FCSTD DOCUMENT  (FreeCAD 0.16R6712 (Git))
Label: Support_Composants
License: All rights reserved
LicenseURL: http://en.wikipedia.org/wiki/All_rights_reserved
objects: Sketcher::SketchObject×20, PartDesign::Pad×12, PartDesign::Pocket×8, Mesh::Feature×6
note: 60 computed .brp shape members not serialized (recipe doc carries the construction recipe); baked Part::Feature solids carry a one-line shape summary decoded from their .brp

FEATURE [Sketcher::SketchObject] Sketch
  sketch-geometry (4):
    g0: LineSegment StartX=0 StartY=1 StartZ=0 EndX=69 EndY=1 EndZ=0
    g1: LineSegment StartX=69 StartY=1 StartZ=0 EndX=69 EndY=0 EndZ=0
    g2: LineSegment StartX=69 StartY=0 StartZ=0 EndX=0 EndY=0 EndZ=0
    g3: LineSegment StartX=0 StartY=0 StartZ=0 EndX=0 EndY=1 EndZ=0
  constraints (11):
    c: Coincident(g0,g1)
    c: Coincident(g1,g2)
    c: Coincident(g2,g3)
    c: Coincident(g3,g0)
    c: Horizontal(g0)
    c: Horizontal(g2)
    c: Vertical(g1)
    c: Vertical(g3)
    c: DistanceX(g2,g2) = 69
    c: DistanceY(g1,g1) = 1
    c: Coincident(g2,g-1)
FEATURE [PartDesign::Pad] Pad
  Length = 120
  Length2 = 100
  Sketch = -> Sketch
  Type = 0
FEATURE [Sketcher::SketchObject] Sketch001
  ExternalGeometry = -> [Pad]
  Placement = pos=(0,1,0) rot=(0,0.707107,0.707107;3.14159rad)
  Support = -> Pad [Face1]
  sketch-geometry (9):
    g0: LineSegment StartX=-69 StartY=26 StartZ=0 EndX=0 EndY=26 EndZ=0
    g1: LineSegment StartX=0 StartY=26 StartZ=0 EndX=0 EndY=24 EndZ=0
    g2: LineSegment StartX=0 StartY=24 StartZ=0 EndX=-69 EndY=24 EndZ=0
    g3: LineSegment StartX=-69 StartY=24 StartZ=0 EndX=-69 EndY=26 EndZ=0
    g4: LineSegment StartX=-69 StartY=96 StartZ=0 EndX=0 EndY=96 EndZ=0
    g5: LineSegment StartX=0 StartY=96 StartZ=0 EndX=0 EndY=94 EndZ=0
    g6: LineSegment StartX=0 StartY=94 StartZ=0 EndX=-69 EndY=94 EndZ=0
    g7: LineSegment StartX=-69 StartY=94 StartZ=0 EndX=-69 EndY=96 EndZ=0
    g8: LineSegment [constr] StartX=-69 StartY=60 StartZ=0 EndX=0 EndY=60 EndZ=0
  constraints (27):
    c: Coincident(g0,g1)
    c: Coincident(g1,g2)
    c: Coincident(g2,g3)
    c: Coincident(g3,g0)
    c: Horizontal(g0)
    c: Horizontal(g2)
    c: Vertical(g1)
    c: Vertical(g3)
    c: Coincident(g4,g5)
    c: Coincident(g5,g6)
    c: Coincident(g6,g7)
    c: Coincident(g7,g4)
    c: Horizontal(g4)
    c: Horizontal(g6)
    c: Vertical(g5)
    c: Vertical(g7)
    c: PointOnObject(g8,g-3)
    c: PointOnObject(g8,g-4)
    c: Symmetric(g-4,g-4,g8)
    c: DistanceY(g7,g7) = 2
    c: DistanceY(g3,g3) = 2
    c: PointOnObject(g4,g-3)
    c: PointOnObject(g4,g-4)
    c: PointOnObject(g0,g-4)
    c: PointOnObject(g0,g-3)
    c: Symmetric(g5,g0,g8)
    c: DistanceY(g0,g5) = 68
FEATURE [PartDesign::Pad] Pad001
  Length = 1
  Length2 = 100
  Sketch = -> Sketch001
  Type = 0
FEATURE [Sketcher::SketchObject] Sketch002
  ExternalGeometry = -> [Pad001]
  Placement = pos=(0,1,0) rot=(0,0.707107,0.707107;3.14159rad)
  Support = -> Pad001 [Face8]
  sketch-geometry (4):
    g0: LineSegment StartX=-2 StartY=94 StartZ=0 EndX=0 EndY=94 EndZ=0
    g1: LineSegment StartX=0 StartY=94 StartZ=0 EndX=0 EndY=26 EndZ=0
    g2: LineSegment StartX=0 StartY=26 StartZ=0 EndX=-2 EndY=26 EndZ=0
    g3: LineSegment StartX=-2 StartY=26 StartZ=0 EndX=-2 EndY=94 EndZ=0
  constraints (12):
    c: Coincident(g0,g1)
    c: Coincident(g1,g2)
    c: Coincident(g2,g3)
    c: Coincident(g3,g0)
    c: Horizontal(g0)
    c: Horizontal(g2)
    c: Vertical(g1)
    c: Vertical(g3)
    c: PointOnObject(g1,g-3)
    c: Coincident(g0,g-3)
    c: Coincident(g1,g-3)
    c: DistanceX(g2,g2) = 2
FEATURE [PartDesign::Pad] Pad002
  Length = 17
  Length2 = 100
  Sketch = -> Sketch002
  Type = 0
FEATURE [Sketcher::SketchObject] Sketch004
  ExternalGeometry = -> [Pad002]
  Placement = pos=(0,18,0) rot=(0,0.707107,0.707107;3.14159rad)
  Support = -> Pad002 [Face22]
  sketch-geometry (5):
    g0: LineSegment StartX=-39 StartY=116 StartZ=0 EndX=0 EndY=116 EndZ=0
    g1: LineSegment StartX=0 StartY=116 StartZ=0 EndX=0 EndY=4 EndZ=0
    g2: LineSegment StartX=0 StartY=4 StartZ=0 EndX=-39 EndY=4 EndZ=0
    g3: LineSegment StartX=-39 StartY=4 StartZ=0 EndX=-39 EndY=116 EndZ=0
    g4: LineSegment [constr] StartX=-39 StartY=60 StartZ=0 EndX=0 EndY=60 EndZ=0
  constraints (15):
    c: Coincident(g0,g1)
    c: Coincident(g1,g2)
    c: Coincident(g2,g3)
    c: Coincident(g3,g0)
    c: Horizontal(g0)
    c: Horizontal(g2)
    c: Vertical(g1)
    c: Vertical(g3)
    c: DistanceY(g3,g3) = 112
    c: DistanceX(g0,g0) = 39
    c: PointOnObject(g4,g3)
    c: Symmetric(g1,g0,g4)
    c: PointOnObject(g-3,g1)
    c: PointOnObject(g4,g-3)
    c: Symmetric(g-3,g-3,g4)
FEATURE [PartDesign::Pad] Pad003
  Length = 2
  Length2 = 100
  Sketch = -> Sketch004
  Type = 0
FEATURE [Sketcher::SketchObject] Sketch005
  ExternalGeometry = -> [Pad003]
  Placement = pos=(0,0,4) rot=(1,0,0;3.14159rad)
  Support = -> Pad003 [Face27]
  sketch-geometry (4):
    g0: LineSegment StartX=0 StartY=-18 StartZ=0 EndX=0 EndY=-1 EndZ=0
    g1: LineSegment StartX=0 StartY=-18 StartZ=0 EndX=39 EndY=-18 EndZ=0
    g2: LineSegment StartX=0 StartY=-1 StartZ=0 EndX=7 EndY=-1 EndZ=0
    g3: ArcOfCircle CenterX=39 CenterY=20.6177 CenterZ=0 NormalX=0 NormalY=0 NormalZ=1 Radius=38.6177 StartAngle=3.73572 EndAngle=4.71239
  constraints (12):
    c: Coincident(g0,g2)
    c: Horizontal(g2)
    c: Coincident(g0,g1)
    c: Horizontal(g1)
    c: Vertical(g0)
    c: DistanceX(g0,g2) = 7
    c: Coincident(g3,g1)
    c: Coincident(g3,g2)
    c: DistanceY(g0,g0) = 17
    c: Coincident(g1,g-3)
    c: Coincident(g0,g-3)
    c: Tangent(g-3,g3)
FEATURE [PartDesign::Pad] Pad004
  Length = 2
  Length2 = 100
  Reversed = true
  Sketch = -> Sketch005
  Type = 0
FEATURE [Sketcher::SketchObject] Sketch006
  ExternalGeometry = -> [Pad004]
  Placement = pos=(0,0,116) rot=(0,0,1;0rad)
  Support = -> Pad004 [Face31]
  sketch-geometry (4):
    g0: LineSegment StartX=0 StartY=18 StartZ=0 EndX=0 EndY=1 EndZ=0
    g1: LineSegment StartX=0 StartY=1 StartZ=0 EndX=7 EndY=1 EndZ=0
    g2: LineSegment StartX=0 StartY=18 StartZ=0 EndX=39 EndY=18 EndZ=0
    g3: ArcOfCircle CenterX=39 CenterY=-20.6177 CenterZ=0 NormalX=0 NormalY=0 NormalZ=1 Radius=38.6177 StartAngle=1.5708 EndAngle=2.54746
  constraints (12):
    c: Vertical(g0)
    c: Coincident(g1,g0)
    c: Horizontal(g1)
    c: Horizontal(g2)
    c: Coincident(g2,g0)
    c: DistanceY(g0,g0) = 17
    c: DistanceX(g1,g1) = 7
    c: Coincident(g3,g2)
    c: Coincident(g3,g1)
    c: Coincident(g2,g-3)
    c: Coincident(g0,g-3)
    c: Tangent(g3,g-3)
FEATURE [PartDesign::Pad] Pad005
  Length = 2
  Length2 = 100
  Reversed = true
  Sketch = -> Sketch006
  Type = 0
FEATURE [Sketcher::SketchObject] Sketch007
  ExternalGeometry = -> [Pad005]
  Placement = pos=(0,0,0) rot=(0.57735,-0.57735,-0.57735;2.0944rad)
  Support = -> Pad005 [Face19]
  sketch-geometry (4):
    g0: LineSegment StartX=-15 StartY=74 StartZ=0 EndX=-2 EndY=74 EndZ=0
    g1: LineSegment StartX=-15 StartY=36 StartZ=0 EndX=-2 EndY=36 EndZ=0
    g2: LineSegment StartX=-15 StartY=74 StartZ=0 EndX=-15 EndY=36 EndZ=0
    g3: LineSegment StartX=-2 StartY=74 StartZ=0 EndX=-2 EndY=36 EndZ=0
  constraints (12):
    c: Horizontal(g0)
    c: Horizontal(g1)
    c: Coincident(g2,g0)
    c: Coincident(g2,g1)
    c: Vertical(g2)
    c: Coincident(g3,g0)
    c: Coincident(g3,g1)
    c: Vertical(g3)
    c: DistanceY(g0,g-3) = 20
    c: DistanceX(g0,g-3) = 1
    c: DistanceY(g-4,g1) = 10
    c: DistanceX(g-4,g1) = 3
FEATURE [PartDesign::Pocket] Pocket
  Length = 5
  Sketch = -> Sketch007
  Type = 2
FEATURE [Sketcher::SketchObject] Sketch008
  ExternalGeometry = -> [Pocket]
  Placement = pos=(0,20,0) rot=(0,0.707107,0.707107;3.14159rad)
  Support = -> Pocket [Face39]
  sketch-geometry (8):
    g0: LineSegment StartX=0 StartY=116 StartZ=0 EndX=-2 EndY=116 EndZ=0
    g1: LineSegment StartX=-2 StartY=116 StartZ=0 EndX=-2 EndY=6 EndZ=0
    g2: LineSegment StartX=0 StartY=4 StartZ=0 EndX=0 EndY=116 EndZ=0
    g3: LineSegment StartX=-39 StartY=4 StartZ=0 EndX=0 EndY=4 EndZ=0
    g4: LineSegment StartX=-2 StartY=6 StartZ=0 EndX=-37 EndY=6 EndZ=0
    g5: LineSegment StartX=-39 StartY=116 StartZ=0 EndX=-37 EndY=116 EndZ=0
    g6: LineSegment StartX=-37 StartY=116 StartZ=0 EndX=-37 EndY=6 EndZ=0
    g7: LineSegment StartX=-39 StartY=116 StartZ=0 EndX=-39 EndY=4 EndZ=0
  constraints (22):
    c: Coincident(g0,g1)
    c: Coincident(g2,g0)
    c: Horizontal(g0)
    c: Vertical(g1)
    c: Vertical(g2)
    c: Horizontal(g3)
    c: Horizontal(g4)
    c: Coincident(g4,g1)
    c: DistanceX(g0,g0) = 2
    c: Coincident(g5,g6)
    c: Horizontal(g5)
    c: Vertical(g6)
    c: Coincident(g4,g6)
    c: DistanceY(g3,g1) = 2
    c: Coincident(g2,g3)
    c: Coincident(g7,g5)
    c: Coincident(g7,g3)
    c: DistanceX(g5,g5) = 2
    c: Coincident(g5,g-4)
    c: Coincident(g0,g-3)
    c: Coincident(g-3,g2)
    c: Coincident(g3,g-4)
FEATURE [PartDesign::Pad] Pad006
  Length = 25
  Length2 = 100
  Sketch = -> Sketch008
  Type = 0
FEATURE [Sketcher::SketchObject] Sketch010
  ExternalGeometry = -> [Pad006]
  Placement = pos=(0,0,0) rot=(0.57735,-0.57735,-0.57735;2.0944rad)
  Support = -> Pad006 [Face12]
  sketch-geometry (5):
    g0: LineSegment StartX=-20 StartY=120 StartZ=0 EndX=-18 EndY=120 EndZ=0
    g1: LineSegment StartX=-18 StartY=120 StartZ=0 EndX=-18 EndY=0 EndZ=0
    g2: LineSegment StartX=-18 StartY=0 StartZ=0 EndX=-20 EndY=0 EndZ=0
    g3: LineSegment StartX=-20 StartY=0 StartZ=0 EndX=-20 EndY=120 EndZ=0
    g4: LineSegment [constr] StartX=-18 StartY=120 StartZ=0 EndX=-1 EndY=120 EndZ=0
  constraints (14):
    c: Coincident(g0,g1)
    c: Coincident(g1,g2)
    c: Coincident(g2,g3)
    c: Coincident(g3,g0)
    c: Horizontal(g0)
    c: Horizontal(g2)
    c: Vertical(g1)
    c: Vertical(g3)
    c: PointOnObject(g1,g-1)
    c: Coincident(g4,g0)
    c: Coincident(g4,g-3)
    c: Horizontal(g4)
    c: DistanceX(g0,g0) = 2
    c: PointOnObject(g-4,g1)
FEATURE [PartDesign::Pad] Pad007
  Length = 100
  Length2 = 100
  Reversed = true
  Sketch = -> Sketch010
  Type = 0
FEATURE [Sketcher::SketchObject] Sketch011
  ExternalGeometry = -> [Pad007]
  Placement = pos=(0,20,0) rot=(0,0.707107,0.707107;3.14159rad)
  Support = -> Pad007 [Face10]
  sketch-geometry (20):
    g0: LineSegment StartX=-69 StartY=10 StartZ=0 EndX=-74 EndY=10 EndZ=0
    g1: LineSegment StartX=-74 StartY=10 StartZ=0 EndX=-74 EndY=5 EndZ=0
    g2: LineSegment StartX=-74 StartY=5 StartZ=0 EndX=-69 EndY=5 EndZ=0
    g3: LineSegment StartX=-69 StartY=5 StartZ=0 EndX=-69 EndY=10 EndZ=0
    g4: LineSegment StartX=-49 StartY=10 StartZ=0 EndX=-44 EndY=10 EndZ=0
    g5: LineSegment StartX=-44 StartY=10 StartZ=0 EndX=-44 EndY=5 EndZ=0
    g6: LineSegment StartX=-44 StartY=5 StartZ=0 EndX=-49 EndY=5 EndZ=0
    g7: LineSegment StartX=-49 StartY=5 StartZ=0 EndX=-49 EndY=10 EndZ=0
    g8: LineSegment StartX=-74 StartY=115 StartZ=0 EndX=-69 EndY=115 EndZ=0
    g9: LineSegment StartX=-69 StartY=115 StartZ=0 EndX=-69 EndY=110 EndZ=0
    g10: LineSegment StartX=-69 StartY=110 StartZ=0 EndX=-74 EndY=110 EndZ=0
    g11: LineSegment StartX=-74 StartY=110 StartZ=0 EndX=-74 EndY=115 EndZ=0
    g12: LineSegment StartX=-49 StartY=115 StartZ=0 EndX=-44 EndY=115 EndZ=0
    g13: LineSegment StartX=-44 StartY=115 StartZ=0 EndX=-44 EndY=110 EndZ=0
    g14: LineSegment StartX=-44 StartY=110 StartZ=0 EndX=-49 EndY=110 EndZ=0
    g15: LineSegment StartX=-49 StartY=110 StartZ=0 EndX=-49 EndY=115 EndZ=0
    g16: LineSegment [constr] StartX=-69 StartY=110 StartZ=0 EndX=-49 EndY=110 EndZ=0
    g17: LineSegment [constr] StartX=-74 StartY=5 StartZ=0 EndX=-49 EndY=5 EndZ=0
    g18: LineSegment [constr] StartX=-69 StartY=10 StartZ=0 EndX=-49 EndY=10 EndZ=0
    g19: LineSegment [constr] StartX=-69 StartY=115 StartZ=0 EndX=-49 EndY=115 EndZ=0
  constraints (56):
    c: Coincident(g0,g1)
    c: Coincident(g1,g2)
    c: Coincident(g2,g3)
    c: Coincident(g3,g0)
    c: Horizontal(g0)
    c: Horizontal(g2)
    c: Vertical(g1)
    c: Vertical(g3)
    c: Coincident(g4,g5)
    c: Coincident(g5,g6)
    c: Coincident(g6,g7)
    c: Coincident(g7,g4)
    c: Horizontal(g4)
    c: Horizontal(g6)
    c: Vertical(g5)
    c: Vertical(g7)
    c: Coincident(g8,g9)
    c: Coincident(g9,g10)
    c: Coincident(g10,g11)
    c: Coincident(g11,g8)
    c: Horizontal(g8)
    c: Horizontal(g10)
    c: Vertical(g9)
    c: Vertical(g11)
    c: Coincident(g12,g13)
    c: Coincident(g13,g14)
    c: Coincident(g14,g15)
    c: Coincident(g15,g12)
    c: Horizontal(g12)
    c: Horizontal(g14)
    c: Vertical(g13)
    c: Vertical(g15)
    c: Coincident(g16,g9)
    c: Coincident(g16,g14)
    c: Horizontal(g16)
    c: Coincident(g17,g1)
    c: Coincident(g17,g6)
    c: Horizontal(g17)
    c: DistanceX(g2,g2) = 5
    c: DistanceX(g6,g6) = 5
    c: DistanceX(g10,g10) = 5
    c: DistanceX(g16,g16) = 20
    c: DistanceX(g14,g14) = 5
    c: DistanceY(g12,g-4) = 5
    c: DistanceY(g-1,g5) = 5
    c: Coincident(g18,g0)
    c: Coincident(g18,g4)
    c: Horizontal(g18)
    c: Coincident(g19,g12)
    c: Horizontal(g19)
    c: Coincident(g19,g8)
    c: DistanceY(g1,g1) = 5
    c: DistanceY(g11,g11) = 5
    c: DistanceX(g0,g4) = 20
    c: DistanceX(g5,g-5) = 5
    c: DistanceX(g12,g-5) = 5
FEATURE [PartDesign::Pad] Pad008
  Length = 10
  Length2 = 100
  Sketch = -> Sketch011
  Type = 0
FEATURE [Mesh::Feature] Servo_CYS
  Placement = pos=(69,20,19) rot=(0,1,0;3.14159rad)
FEATURE [Mesh::Feature] Servo_CYS001
  Placement = pos=(49,20,101) rot=(0,0,1;0rad)
FEATURE [Mesh::Feature] ESC
  Placement = pos=(67,1,94) rot=(-1,0,0;1.5708rad)
FEATURE [Sketcher::SketchObject] Sketch012
  ExternalGeometry = -> [Pad008]
  Placement = pos=(0,20,0) rot=(0,0.707107,0.707107;3.14159rad)
  Support = -> Pad008 [Face10]
  sketch-geometry (7):
    g0: Circle CenterX=-85 CenterY=75.25 CenterZ=0 NormalX=0 NormalY=0 NormalZ=1 Radius=4
    g1: Circle CenterX=-54.5 CenterY=75.25 CenterZ=0 NormalX=0 NormalY=0 NormalZ=1 Radius=4
    g2: Circle CenterX=-85 CenterY=44.75 CenterZ=0 NormalX=0 NormalY=0 NormalZ=1 Radius=4
    g3: Circle CenterX=-54.5 CenterY=44.75 CenterZ=0 NormalX=0 NormalY=0 NormalZ=1 Radius=4
    g4: LineSegment [constr] StartX=-85 StartY=75.25 StartZ=0 EndX=-54.5 EndY=75.25 EndZ=0
    g5: LineSegment [constr] StartX=-85 StartY=75.25 StartZ=0 EndX=-85 EndY=44.75 EndZ=0
    g6: LineSegment [constr] StartX=-100 StartY=60 StartZ=0 EndX=0 EndY=60 EndZ=0
  constraints (19):
    c: DistanceY(g3,g1) = 30.5
    c: DistanceX(g2,g3) = 30.5
    c: DistanceY(g2,g0) = 30.5
    c: DistanceX(g0,g1) = 30.5
    c: Coincident(g4,g0)
    c: Coincident(g4,g1)
    c: Coincident(g5,g0)
    c: Coincident(g5,g2)
    c: Vertical(g5)
    c: Horizontal(g4)
    c: Radius(g0) = 4
    c: Equal(g0,g1)
    c: Equal(g0,g3)
    c: Equal(g0,g2)
    c: PointOnObject(g6,g-2)
    c: PointOnObject(g6,g-5)
    c: Symmetric(g2,g0,g6)
    c: Symmetric(g-5,g-5,g6)
    c: DistanceX(g-5,g0) = 15
FEATURE [PartDesign::Pad] Pad009
  Length = 4
  Length2 = 100
  Sketch = -> Sketch012
  Type = 0
FEATURE [Sketcher::SketchObject] Sketch013
  ExternalGeometry = -> [Pad009]
  Placement = pos=(0,0,0) rot=(1,0,0;1.5708rad)
  Support = -> Pad009 [Face68]
  sketch-geometry (7):
    g0: Circle CenterX=54.5 CenterY=75.25 CenterZ=0 NormalX=0 NormalY=0 NormalZ=1 Radius=3
    g1: Circle CenterX=85 CenterY=75.25 CenterZ=0 NormalX=0 NormalY=0 NormalZ=1 Radius=3
    g2: Circle CenterX=54.5 CenterY=44.75 CenterZ=0 NormalX=0 NormalY=0 NormalZ=1 Radius=3
    g3: Circle CenterX=85 CenterY=44.75 CenterZ=0 NormalX=0 NormalY=0 NormalZ=1 Radius=3
    g4: LineSegment [constr] StartX=54.5 StartY=44.75 StartZ=0 EndX=85 EndY=44.75 EndZ=0
    g5: LineSegment [constr] StartX=54.5 StartY=75.25 StartZ=0 EndX=54.5 EndY=44.75 EndZ=0
    g6: LineSegment [constr] StartX=0 StartY=60 StartZ=0 EndX=100 EndY=60 EndZ=0
  constraints (19):
    c: Coincident(g4,g2)
    c: Coincident(g4,g3)
    c: Coincident(g5,g0)
    c: Coincident(g5,g2)
    c: Vertical(g5)
    c: Horizontal(g4)
    c: DistanceY(g3,g1) = 30.5
    c: DistanceX(g4,g4) = 30.5
    c: DistanceY(g5,g5) = 30.5
    c: DistanceX(g0,g1) = 30.5
    c: PointOnObject(g6,g-3)
    c: PointOnObject(g6,g-4)
    c: Symmetric(g-4,g-4,g6)
    c: Symmetric(g3,g1,g6)
    c: Radius(g1) = 3
    c: Equal(g1,g2)
    c: Equal(g1,g3)
    c: Equal(g1,g0)
    c: DistanceX(g1,g-4) = 15
FEATURE [PartDesign::Pocket] Pocket001
  Length = 21
  Sketch = -> Sketch013
  Type = 0
FEATURE [Sketcher::SketchObject] Sketch014
  ExternalGeometry = -> [Pocket001]
  Placement = pos=(0,24,0) rot=(0,0.707107,0.707107;3.14159rad)
  Support = -> Pocket001 [Face49]
  sketch-geometry (4):
    g0: Circle CenterX=-85 CenterY=75.25 CenterZ=0 NormalX=0 NormalY=0 NormalZ=1 Radius=1.7
    g1: Circle CenterX=-54.5 CenterY=75.25 CenterZ=0 NormalX=0 NormalY=0 NormalZ=1 Radius=1.7
    g2: Circle CenterX=-85 CenterY=44.75 CenterZ=0 NormalX=0 NormalY=0 NormalZ=1 Radius=1.7
    g3: Circle CenterX=-54.5 CenterY=44.75 CenterZ=0 NormalX=0 NormalY=0 NormalZ=1 Radius=1.7
  constraints (8):
    c: Coincident(g0,g-3)
    c: Coincident(g1,g-4)
    c: Coincident(g2,g-5)
    c: Coincident(g3,g-6)
    c: Radius(g3) = 1.7
    c: Equal(g3,g1)
    c: Equal(g3,g0)
    c: Equal(g3,g2)
FEATURE [PartDesign::Pocket] Pocket002
  Length = 5
  Sketch = -> Sketch014
  Type = 1
FEATURE [Mesh::Feature] Carte_SPRACINGF3
  Placement = pos=(88,24,42) rot=(0,0.707107,0.707107;3.14159rad)
FEATURE [Mesh::Feature] Recepteur
  Placement = pos=(43,27,19) rot=(1,0,0;1.5708rad)
FEATURE [Mesh::Feature] Batterie
  Placement = pos=(3,23,6) rot=(0,0,1;0rad)
FEATURE [Sketcher::SketchObject] Sketch015
  ExternalGeometry = -> [Pocket002]
  Placement = pos=(0,0,120) rot=(0,0,1;0rad)
  Support = -> Pocket002 [Face78]
  sketch-geometry (4):
    g0: LineSegment StartX=62.2327 StartY=4.2e-11 StartZ=0 EndX=100 EndY=0 EndZ=0
    g1: LineSegment StartX=100 StartY=0 StartZ=0 EndX=100 EndY=18 EndZ=0
    g2: LineSegment StartX=85 StartY=18 StartZ=0 EndX=100 EndY=18 EndZ=0
    g3: ArcOfCircle CenterX=62.2326 CenterY=23.3987 CenterZ=0 NormalX=0 NormalY=0 NormalZ=1 Radius=23.3987 StartAngle=4.71239 EndAngle=6.05036
  constraints (12):
    c: PointOnObject(g0,g-1)
    c: Coincident(g1,g0)
    c: Vertical(g1)
    c: Coincident(g1,g-3)
    c: PointOnObject(g2,g-3)
    c: Coincident(g2,g1)
    c: PointOnObject(g0,g-4)
    c: Coincident(g3,g2)
    c: Coincident(g3,g0)
    c: Tangent(g3,g0)
    c: PointOnObject(g-5,g3)
    c: DistanceX(g2,g1) = 15
FEATURE [PartDesign::Pad] Pad010
  Length = 2
  Length2 = 100
  Reversed = true
  Sketch = -> Sketch015
  Type = 0
FEATURE [Sketcher::SketchObject] Sketch016
  ExternalGeometry = -> [Pad010]
  Placement = pos=(0,0,0) rot=(1,0,0;3.14159rad)
  Support = -> Pad010 [Face83]
  sketch-geometry (4):
    g0: LineSegment StartX=62.2326 StartY=0 StartZ=0 EndX=100 EndY=0 EndZ=0
    g1: LineSegment StartX=100 StartY=0 StartZ=0 EndX=100 EndY=-18 EndZ=0
    g2: LineSegment StartX=100 StartY=-18 StartZ=0 EndX=85 EndY=-18 EndZ=0
    g3: ArcOfCircle CenterX=62.2326 CenterY=-23.3987 CenterZ=0 NormalX=0 NormalY=0 NormalZ=1 Radius=23.3987 StartAngle=0.232825 EndAngle=1.5708
  constraints (14):
    c: PointOnObject(g0,g-1)
    c: PointOnObject(g0,g-1)
    c: Vertical(g1)
    c: Horizontal(g2)
    c: PointOnObject(g3,g0)
    c: Coincident(g3,g0)
    c: Coincident(g3,g2)
    c: PointOnObject(g-6,g3)
    c: Tangent(g3,g0)
    c: PointOnObject(g2,g-3)
    c: Coincident(g2,g1)
    c: Coincident(g2,g-3)
    c: DistanceX(g2,g1) = 15
    c: Coincident(g0,g1)
FEATURE [PartDesign::Pad] Pad011
  Length = 2
  Length2 = 100
  Reversed = true
  Sketch = -> Sketch016
  Type = 0
FEATURE [Sketcher::SketchObject] Sketch017
  ExternalGeometry = -> [Pad011]
  Placement = pos=(0,0,0) rot=(1,0,0;3.14159rad)
  Support = -> Pad011 [Face43]
  sketch-geometry (4):
    g0: LineSegment StartX=90 StartY=0 StartZ=0 EndX=100 EndY=0 EndZ=0
    g1: LineSegment StartX=100 StartY=0 StartZ=0 EndX=100 EndY=-20 EndZ=0
    g2: LineSegment StartX=100 StartY=-20 StartZ=0 EndX=90 EndY=-20 EndZ=0
    g3: LineSegment StartX=90 StartY=-20 StartZ=0 EndX=90 EndY=0 EndZ=0
  constraints (11):
    c: Coincident(g0,g1)
    c: Coincident(g1,g2)
    c: Coincident(g2,g3)
    c: Coincident(g3,g0)
    c: Horizontal(g0)
    c: Horizontal(g2)
    c: Vertical(g1)
    c: Vertical(g3)
    c: PointOnObject(g0,g-1)
    c: Coincident(g1,g-4)
    c: DistanceX(g2,g1) = 10
FEATURE [PartDesign::Pocket] Pocket003
  Length = 5
  Sketch = -> Sketch017
  Type = 1
FEATURE [Sketcher::SketchObject] Sketch018
  ExternalGeometry = -> [Pocket003]
  Placement = pos=(0,0,115) rot=(0,0,1;0rad)
  Support = -> Pocket003 [Face32]
  sketch-geometry (3):
    g0: Circle CenterX=47.4 CenterY=24.2 CenterZ=0 NormalX=0 NormalY=0 NormalZ=1 Radius=0.75
    g1: Circle CenterX=70.4 CenterY=24.2 CenterZ=0 NormalX=0 NormalY=0 NormalZ=1 Radius=0.75
    g2: LineSegment [constr] StartX=47.4 StartY=24.2 StartZ=0 EndX=70.4 EndY=24.2 EndZ=0
  constraints (8):
    c: Radius(g1) = 0.75
    c: Radius(g0) = 0.75
    c: DistanceX(g0,g1) = 23
    c: DistanceX(g-4,g1) = 1.4
    c: Coincident(g2,g0)
    c: Coincident(g2,g1)
    c: Horizontal(g2)
    c: DistanceY(g0,g-3) = 5.8
FEATURE [PartDesign::Pocket] Pocket004
  Length = 5
  Sketch = -> Sketch018
  Type = 1
FEATURE [Sketcher::SketchObject] Sketch019
  ExternalGeometry = -> [Pocket004]
  Placement = pos=(0,20,0) rot=(0,0.707107,0.707107;3.14159rad)
  Support = -> Pocket004 [Face10]
  sketch-geometry (17):
    g0: LineSegment StartX=-77 StartY=100 StartZ=0 EndX=-41 EndY=100 EndZ=0
    g1: LineSegment StartX=-41 StartY=100 StartZ=0 EndX=-41 EndY=82 EndZ=0
    g2: LineSegment StartX=-41 StartY=82 StartZ=0 EndX=-86 EndY=82 EndZ=0
    g3: LineSegment StartX=-86 StartY=82 StartZ=0 EndX=-86 EndY=100 EndZ=0
    g4: LineSegment StartX=-86 StartY=67 StartZ=0 EndX=-41 EndY=67 EndZ=0
    g5: LineSegment StartX=-41 StartY=67 StartZ=0 EndX=-41 EndY=52 EndZ=0
    g6: LineSegment StartX=-41 StartY=52 StartZ=0 EndX=-86 EndY=52 EndZ=0
    g7: LineSegment StartX=-86 StartY=52 StartZ=0 EndX=-86 EndY=67 EndZ=0
    g8: LineSegment StartX=-77 StartY=100 StartZ=0 EndX=-77 EndY=116 EndZ=0
    g9: LineSegment StartX=-77 StartY=116 StartZ=0 EndX=-86 EndY=116 EndZ=0
    g10: LineSegment StartX=-86 StartY=116 StartZ=0 EndX=-86 EndY=100 EndZ=0
    g11: LineSegment StartX=-86 StartY=4 StartZ=0 EndX=-86 EndY=37 EndZ=0
    g12: LineSegment StartX=-86 StartY=37 StartZ=0 EndX=-45 EndY=37 EndZ=0
    g13: LineSegment StartX=-45 StartY=37 StartZ=0 EndX=-45 EndY=22 EndZ=0
    g14: LineSegment StartX=-77 StartY=22 StartZ=0 EndX=-45 EndY=22 EndZ=0
    g15: LineSegment StartX=-77 StartY=22 StartZ=0 EndX=-77 EndY=4 EndZ=0
    g16: LineSegment StartX=-77 StartY=4 StartZ=0 EndX=-86 EndY=4 EndZ=0
  constraints (52):
    c: Coincident(g0,g1)
    c: Coincident(g1,g2)
    c: Coincident(g2,g3)
    c: Horizontal(g0)
    c: Horizontal(g2)
    c: Vertical(g1)
    c: Vertical(g3)
    c: DistanceX(g-3,g3) = 4
    c: DistanceX(g0,g-5) = 2
    c: DistanceY(g3,g-3) = 20
    c: DistanceY(g3,g3) = 18
    c: Coincident(g4,g5)
    c: Coincident(g5,g6)
    c: Coincident(g6,g7)
    c: Coincident(g7,g4)
    c: Horizontal(g4)
    c: Horizontal(g6)
    c: Vertical(g5)
    c: Vertical(g7)
    c: DistanceY(g4,g2) = 15
    c: DistanceX(g4,g-5) = 2
    c: DistanceX(g-3,g4) = 4
    c: DistanceY(g7,g7) = 15
    c: Coincident(g8,g9)
    c: Coincident(g9,g10)
    c: Horizontal(g9)
    c: Vertical(g8)
    c: Vertical(g10)
    c: PointOnObject(g0,g8)
    c: DistanceY(g9,g-3) = 4
    c: DistanceX(g9,g9) = 9
    c: Coincident(g3,g10)
    c: Coincident(g0,g8)
    c: DistanceY(g8,g8) = 16
    c: Coincident(g12,g11)
    c: Horizontal(g12)
    c: Vertical(g13)
    c: Horizontal(g14)
    c: Coincident(g16,g11)
    c: Vertical(g11)
    c: Coincident(g14,g15)
    c: Vertical(g15)
    c: Coincident(g15,g16)
    c: Horizontal(g16)
    c: DistanceX(g-3,g11) = 4
    c: DistanceY(g11,g6) = 15
    c: Coincident(g13,g12)
    c: Coincident(g14,g13)
    c: DistanceY(g13,g13) = 15
    c: DistanceY(g-3,g11) = 4
    c: DistanceX(g16,g16) = 9
    c: DistanceX(g13,g-5) = 6
FEATURE [PartDesign::Pocket] Pocket005
  Length = 0
  Sketch = -> Sketch019
  Type = 2
FEATURE [Sketcher::SketchObject] Sketch020
  ExternalGeometry = -> [Pocket005]
  Placement = pos=(0,20,0) rot=(0,0.707107,0.707107;3.14159rad)
  Support = -> Pocket005 [Face12]
  sketch-geometry (4):
    g0: LineSegment StartX=-32 StartY=106 StartZ=0 EndX=-7 EndY=106 EndZ=0
    g1: LineSegment StartX=-7 StartY=106 StartZ=0 EndX=-7 EndY=16 EndZ=0
    g2: LineSegment StartX=-7 StartY=16 StartZ=0 EndX=-32 EndY=16 EndZ=0
    g3: LineSegment StartX=-32 StartY=16 StartZ=0 EndX=-32 EndY=106 EndZ=0
  constraints (12):
    c: Coincident(g0,g1)
    c: Coincident(g1,g2)
    c: Coincident(g2,g3)
    c: Coincident(g3,g0)
    c: Horizontal(g0)
    c: Horizontal(g2)
    c: Vertical(g1)
    c: Vertical(g3)
    c: DistanceY(g0,g-3) = 10
    c: DistanceX(g0,g-3) = 5
    c: DistanceX(g-4,g0) = 5
    c: DistanceY(g-4,g2) = 10
FEATURE [PartDesign::Pocket] Pocket006
  Length = 5
  Sketch = -> Sketch020
  Type = 2
FEATURE [Sketcher::SketchObject] Sketch021
  ExternalGeometry = -> [Pocket006]
  Placement = pos=(0,0,0) rot=(1,0,0;1.5708rad)
  Support = -> Pocket006 [Face114]
  sketch-geometry (5):
    g0: LineSegment StartX=5 StartY=87.5 StartZ=0 EndX=60 EndY=87.5 EndZ=0
    g1: LineSegment StartX=60 StartY=87.5 StartZ=0 EndX=60 EndY=32.5 EndZ=0
    g2: LineSegment StartX=60 StartY=32.5 StartZ=0 EndX=5 EndY=32.5 EndZ=0
    g3: LineSegment StartX=5 StartY=32.5 StartZ=0 EndX=5 EndY=87.5 EndZ=0
    g4: LineSegment [constr] StartX=0 StartY=60 StartZ=0 EndX=69 EndY=60 EndZ=0
  constraints (15):
    c: Coincident(g0,g1)
    c: Coincident(g1,g2)
    c: Coincident(g2,g3)
    c: Coincident(g3,g0)
    c: Horizontal(g0)
    c: Horizontal(g2)
    c: Vertical(g1)
    c: Vertical(g3)
    c: DistanceY(g1,g1) = 55
    c: DistanceX(g2,g2) = 55
    c: DistanceX(g-3,g0) = 5
    c: PointOnObject(g4,g-3)
    c: PointOnObject(g4,g-4)
    c: Symmetric(g-1,g-3,g4)
    c: Symmetric(g0,g2,g4)
FEATURE [PartDesign::Pocket] Pocket007
  Length = 5
  Sketch = -> Sketch021
  Type = 2
